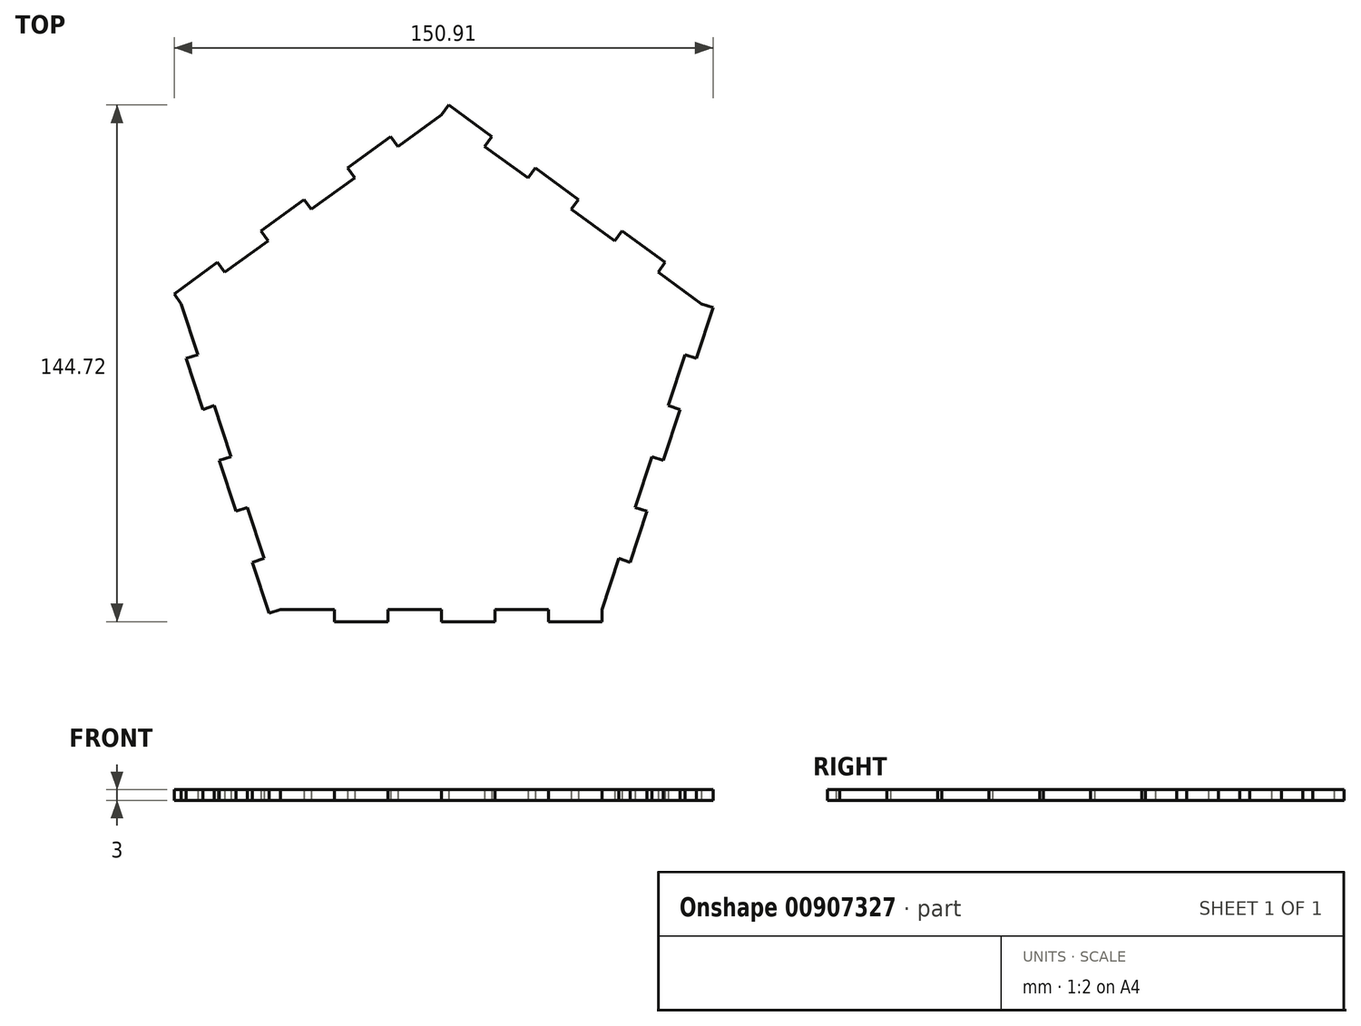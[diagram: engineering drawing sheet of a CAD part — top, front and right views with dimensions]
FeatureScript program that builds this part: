
annotation { "Feature Type Name" : "Feature", "Feature Type Description" : "" }
export const myFeature = defineFeature(function(context is Context, id is Id, definition is map)
    precondition{}
    {
        {
            var Q0;
            Q0=qCreatedBy(makeId("Top.planeOp"),FACE);
            var sketch = newSketch(context, id + "F0", { "sketchPlane" : qUnion([Q0])});
            skCircle(sketch, "E0.cCircle", {"center": v(0, 0) * mm, "radius": 61.94 * mm, "construction": true});
            skLineSegment(sketch, "E0.0", {"start": v(68.18, 9.4) * mm, "end": v(63.54, -4.87) * mm});
            skLineSegment(sketch, "E0.1", {"start": v(30, -61.94) * mm, "end": v(15, -61.94) * mm});
            skLineSegment(sketch, "E0.2", {"start": v(-49.64, -47.67) * mm, "end": v(-54.27, -33.4) * mm});
            skLineSegment(sketch, "E0.3", {"start": v(-60.68, 32.47) * mm, "end": v(-48.54, 41.3) * mm});
            skLineSegment(sketch, "E0.4", {"start": v(12.14, 67.74) * mm, "end": v(24.27, 58.93) * mm});
            skPoint(sketch, "E0.0.midPoint", {"position": v(58.9, -19.14) * mm});
            skCircle(sketch, "E1.cCircle", {"center": v(0, 0) * mm, "radius": 65.38 * mm, "construction": true});
            skLineSegment(sketch, "E1.0", {"start": v(2.02, 79.34) * mm, "end": v(14.16, 70.53) * mm});
            skLineSegment(sketch, "E1.1", {"start": v(76.08, 22.6) * mm, "end": v(71.45, 8.33) * mm});
            skLineSegment(sketch, "E1.2", {"start": v(45, -65.38) * mm, "end": v(30, -65.38) * mm});
            skLineSegment(sketch, "E1.3", {"start": v(-48.27, -63) * mm, "end": v(-52.9, -48.73) * mm});
            skLineSegment(sketch, "E1.4", {"start": v(-74.83, 26.44) * mm, "end": v(-62.7, 35.26) * mm});
            skPoint(sketch, "E1.0.midPoint", {"position": v(38.43, 52.9) * mm});
            skLineSegment(sketch, "E2", {"start": v(-72.81, 23.66) * mm, "end": v(-74.83, 26.44) * mm});
            skLineSegment(sketch, "E3", {"start": v(-62.7, 35.26) * mm, "end": v(-60.68, 32.47) * mm});
            skLineSegment(sketch, "E4", {"start": v(-48.54, 41.3) * mm, "end": v(-50.56, 44.08) * mm});
            skLineSegment(sketch, "E5", {"start": v(-50.56, 44.08) * mm, "end": v(-38.43, 52.9) * mm});
            skLineSegment(sketch, "E6", {"start": v(-38.43, 52.9) * mm, "end": v(-36.4, 50.1) * mm});
            skLineSegment(sketch, "E7", {"start": v(-36.4, 50.1) * mm, "end": v(-24.27, 58.93) * mm});
            skLineSegment(sketch, "E8", {"start": v(-24.27, 58.93) * mm, "end": v(-26.3, 61.7) * mm});
            skLineSegment(sketch, "E9", {"start": v(-26.3, 61.7) * mm, "end": v(-14.16, 70.53) * mm});
            skLineSegment(sketch, "E10", {"start": v(-14.16, 70.53) * mm, "end": v(-12.14, 67.74) * mm});
            skLineSegment(sketch, "E11", {"start": v(0, 76.56) * mm, "end": v(2.02, 79.34) * mm});
            skLineSegment(sketch, "E12", {"start": v(14.16, 70.53) * mm, "end": v(12.14, 67.74) * mm});
            skLineSegment(sketch, "E13", {"start": v(24.27, 58.93) * mm, "end": v(26.3, 61.7) * mm});
            skLineSegment(sketch, "E14", {"start": v(26.3, 61.7) * mm, "end": v(38.43, 52.9) * mm});
            skLineSegment(sketch, "E15", {"start": v(38.43, 52.9) * mm, "end": v(36.4, 50.1) * mm});
            skLineSegment(sketch, "E16", {"start": v(36.4, 50.1) * mm, "end": v(48.54, 41.3) * mm});
            skLineSegment(sketch, "E17", {"start": v(48.54, 41.3) * mm, "end": v(50.56, 44.08) * mm});
            skLineSegment(sketch, "E18", {"start": v(50.56, 44.08) * mm, "end": v(62.7, 35.26) * mm});
            skLineSegment(sketch, "E19", {"start": v(62.7, 35.26) * mm, "end": v(60.68, 32.47) * mm});
            skPoint(sketch, "E20.orphan", {"position": v(0, 80.81) * mm});
            skLineSegment(sketch, "E21", {"start": v(72.81, 23.66) * mm, "end": v(76.08, 22.6) * mm});
            skLineSegment(sketch, "E22", {"start": v(71.45, 8.33) * mm, "end": v(68.18, 9.4) * mm});
            skLineSegment(sketch, "E23", {"start": v(63.54, -4.87) * mm, "end": v(66.81, -5.94) * mm});
            skLineSegment(sketch, "E24", {"start": v(66.81, -5.94) * mm, "end": v(62.18, -20.2) * mm});
            skLineSegment(sketch, "E25", {"start": v(62.18, -20.2) * mm, "end": v(58.9, -19.14) * mm});
            skLineSegment(sketch, "E26", {"start": v(54.27, -33.4) * mm, "end": v(57.54, -34.47) * mm});
            skLineSegment(sketch, "E27", {"start": v(49.64, -47.67) * mm, "end": v(52.9, -48.73) * mm});
            skPoint(sketch, "E28.orphan", {"position": v(76.86, 24.97) * mm});
            skLineSegment(sketch, "E29.trimOffspring", {"start": v(57.54, -34.47) * mm, "end": v(52.9, -48.73) * mm});
            skLineSegment(sketch, "E30.trimOffspring", {"start": v(-12.14, 67.74) * mm, "end": v(0, 76.56) * mm});
            skLineSegment(sketch, "E31.trimOffspring", {"start": v(60.68, 32.47) * mm, "end": v(72.81, 23.66) * mm});
            skLineSegment(sketch, "E32.trimOffspring", {"start": v(58.9, -19.14) * mm, "end": v(54.27, -33.4) * mm});
            skLineSegment(sketch, "E33.trimOffspring", {"start": v(49.64, -47.67) * mm, "end": v(45, -61.94) * mm});
            skLineSegment(sketch, "E34", {"start": v(45, -61.94) * mm, "end": v(45, -65.38) * mm});
            skLineSegment(sketch, "E35", {"start": v(30, -65.38) * mm, "end": v(30, -61.94) * mm});
            skLineSegment(sketch, "E36", {"start": v(15, -61.94) * mm, "end": v(15, -65.38) * mm});
            skLineSegment(sketch, "E37", {"start": v(15, -65.38) * mm, "end": v(0, -65.38) * mm});
            skLineSegment(sketch, "E38", {"start": v(0, -65.38) * mm, "end": v(0, -61.94) * mm});
            skLineSegment(sketch, "E39", {"start": v(0, -61.94) * mm, "end": v(-15, -61.94) * mm});
            skLineSegment(sketch, "E40", {"start": v(-15, -61.94) * mm, "end": v(-15, -65.38) * mm});
            skLineSegment(sketch, "E41", {"start": v(-15, -65.38) * mm, "end": v(-30, -65.38) * mm});
            skLineSegment(sketch, "E42", {"start": v(-30, -65.38) * mm, "end": v(-30, -61.94) * mm});
            skPoint(sketch, "E43.orphan", {"position": v(47.5, -65.38) * mm});
            skLineSegment(sketch, "E44.trimOffspring", {"start": v(-30, -61.94) * mm, "end": v(-45, -61.94) * mm});
            skLineSegment(sketch, "E45", {"start": v(-45, -61.94) * mm, "end": v(-48.27, -63) * mm});
            skLineSegment(sketch, "E46", {"start": v(-52.9, -48.73) * mm, "end": v(-49.64, -47.67) * mm});
            skLineSegment(sketch, "E47", {"start": v(-54.27, -33.4) * mm, "end": v(-57.54, -34.47) * mm});
            skLineSegment(sketch, "E48", {"start": v(-57.54, -34.47) * mm, "end": v(-62.18, -20.2) * mm});
            skLineSegment(sketch, "E49", {"start": v(-62.18, -20.2) * mm, "end": v(-58.9, -19.14) * mm});
            skLineSegment(sketch, "E50", {"start": v(-58.9, -19.14) * mm, "end": v(-63.54, -4.87) * mm});
            skLineSegment(sketch, "E51", {"start": v(-63.54, -4.87) * mm, "end": v(-66.81, -5.94) * mm});
            skLineSegment(sketch, "E52", {"start": v(-66.81, -5.94) * mm, "end": v(-71.45, 8.33) * mm});
            skLineSegment(sketch, "E53", {"start": v(-71.45, 8.33) * mm, "end": v(-68.18, 9.4) * mm});
            skPoint(sketch, "E54.orphan", {"position": v(-47.5, -65.38) * mm});
            skPoint(sketch, "E55.orphan", {"position": v(-76.86, 24.97) * mm});
            skLineSegment(sketch, "E56.trimOffspring", {"start": v(-68.18, 9.4) * mm, "end": v(-72.81, 23.66) * mm});
            skSolve(sketch);
        }
        {
            var Q0;
            Q0=makeQuery(id+"F0.imprint","IMPRINT",FACE,{"disambiguationData":[TD([[makeQuery(id+"F0.imprint","IMPRINT",EDGE,{"derivedFrom":sQuery(id+"F0.wireOp",EDGE,"E2")}),-1.0]])]});
            extrude(context, id + "F1", {"entities" : qUnion([Q0]), "depth" : 3 * mm, "offsetDistance" : 25 * mm});
        }
    });
